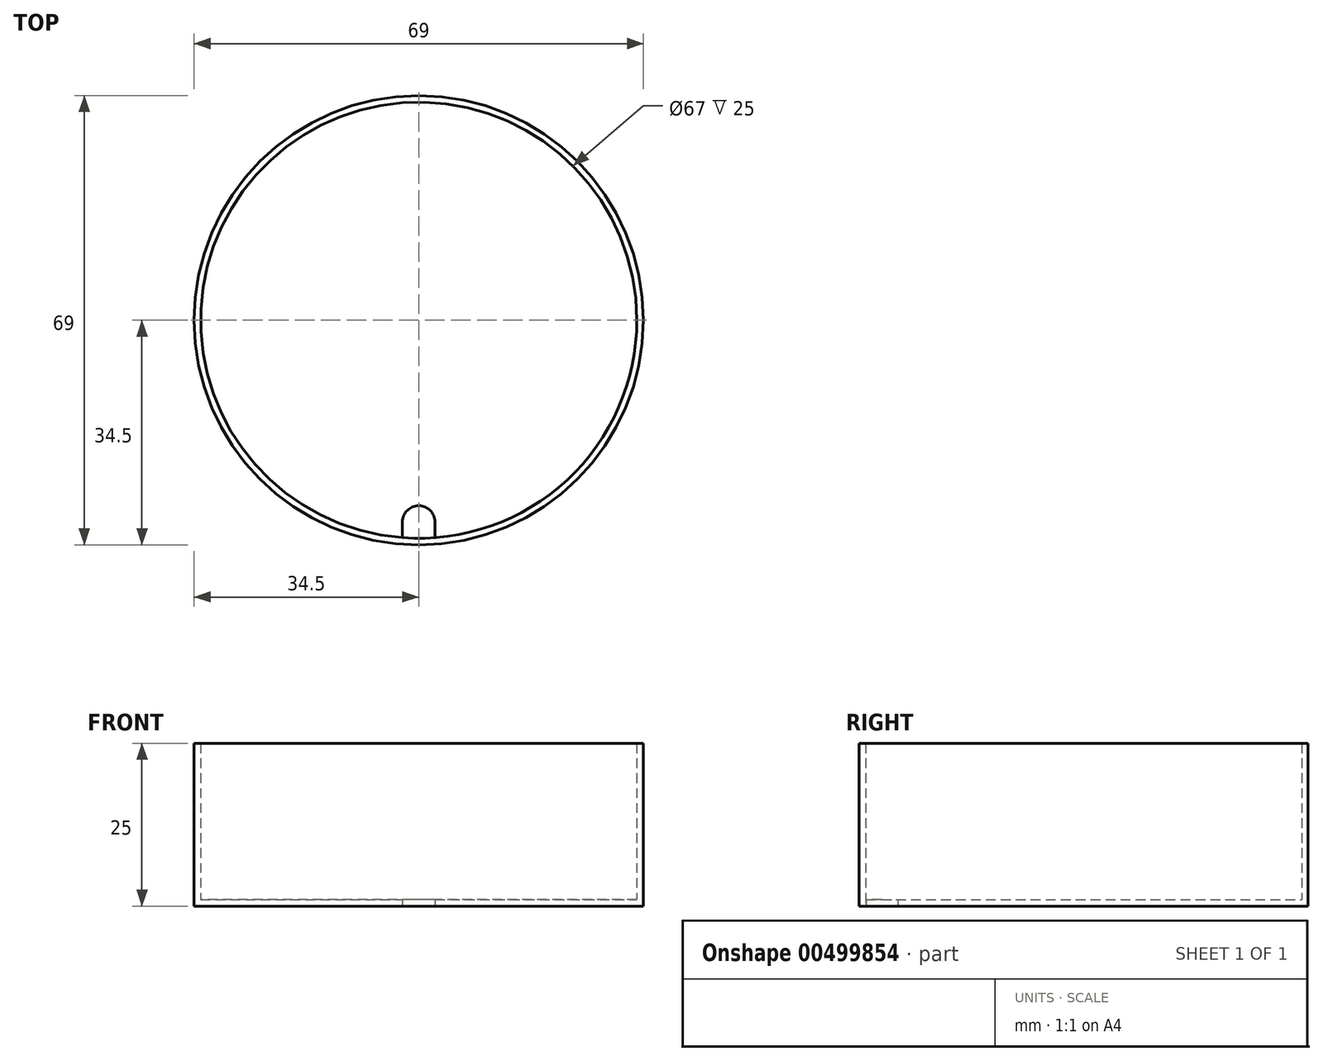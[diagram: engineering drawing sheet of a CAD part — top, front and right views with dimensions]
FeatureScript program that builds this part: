
annotation { "Feature Type Name" : "Feature", "Feature Type Description" : "" }
export const myFeature = defineFeature(function(context is Context, id is Id, definition is map)
    precondition{}
    {
        {
            var Q0;
            Q0=qCreatedBy(makeId("Top.planeOp"),FACE);
            var sketch = newSketch(context, id + "F0", { "sketchPlane" : qUnion([Q0])});
            skCircle(sketch, "E0", {"center": v(0, 0) * mm, "radius": 33.5 * mm});
            skCircle(sketch, "E1.0", {"center": v(0, 0) * mm, "radius": 34.5 * mm});
            skArc(sketch, "E2", {"start": v(2.5, -31) * mm, "mid": v(0, -28.5) * mm, "end": v(-2.5, -31) * mm});
            skLineSegment(sketch, "E3", {"start": v(-2.5, -31) * mm, "end": v(-2.5, -33.4) * mm});
            skLineSegment(sketch, "E4.MirrorCS", {"start": v(2.5, -31) * mm, "end": v(2.5, -33.4) * mm});
            skSolve(sketch);
        }
        {
            var Q0;
            Q0=makeQuery(id+"F0.imprint","IMPRINT",FACE,{"disambiguationData":[TD([[makeQuery(id+"F0.imprint","IMPRINT",EDGE,{"derivedFrom":sQuery(id+"F0.wireOp",EDGE,"E1.0")}),1.0]])]});
            var Q1;
            Q1=makeQuery(id+"F0.imprint","IMPRINT",FACE,{"disambiguationData":[TD([[makeQuery(id+"F0.imprint","IMPRINT",EDGE,{"derivedFrom":sQuery(id+"F0.wireOp",EDGE,"E2")}),-1.0]])]});
            extrude(context, id + "F1", {"entities" : qUnion([Q0, Q1]), "depth" : 1 * mm});
        }
        {
            var Q0;
            Q0 = qSketchRegion(id + "F0", true);
            extrude(context, id + "F2", {"entities" : qUnion([Q0]), "operationType" : NewBodyOperationType.ADD, "depth" : 25 * mm});
        }
    });
